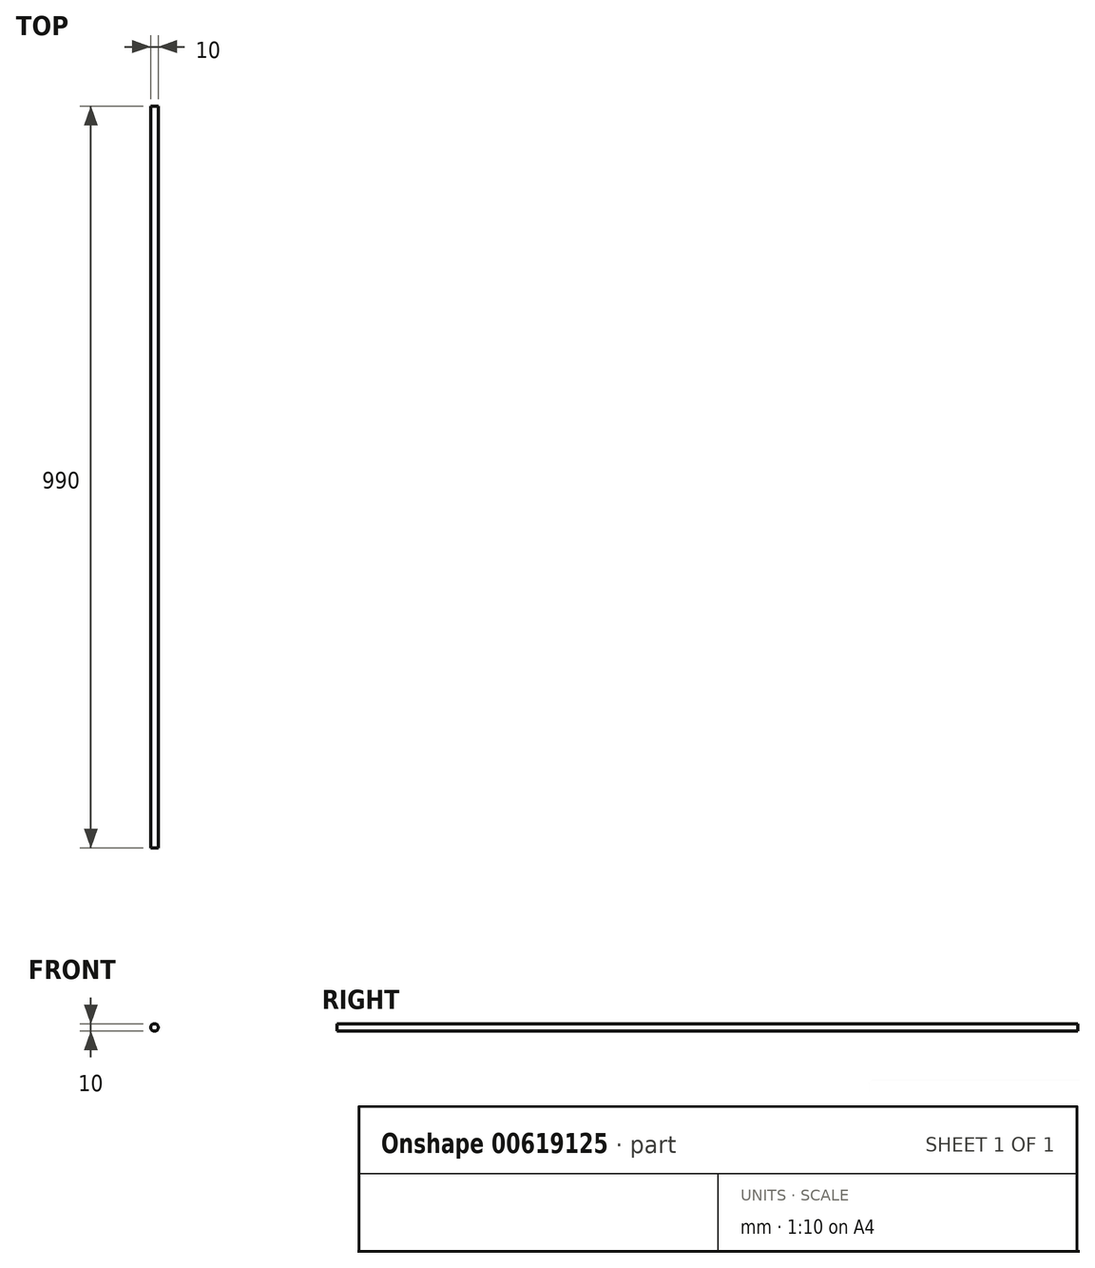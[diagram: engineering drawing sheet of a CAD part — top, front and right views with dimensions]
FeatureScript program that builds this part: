
annotation { "Feature Type Name" : "Feature", "Feature Type Description" : "" }
export const myFeature = defineFeature(function(context is Context, id is Id, definition is map)
    precondition{}
    {
        {
            var Q0;
            Q0=qCreatedBy(makeId("Front.planeOp"),FACE);
            var sketch = newSketch(context, id + "F0", { "sketchPlane" : qUnion([Q0])});
            skCircle(sketch, "E0", {"center": v(0, 0) * mm, "radius": 5 * mm});
            skSolve(sketch);
        }
        {
            var Q0;
            Q0 = qSketchRegion(id + "F0", true);
            extrude(context, id + "F1", {"entities" : qUnion([Q0]), "depth" : 990 * mm, "offsetDistance" : 25 * mm});
        }
    });
